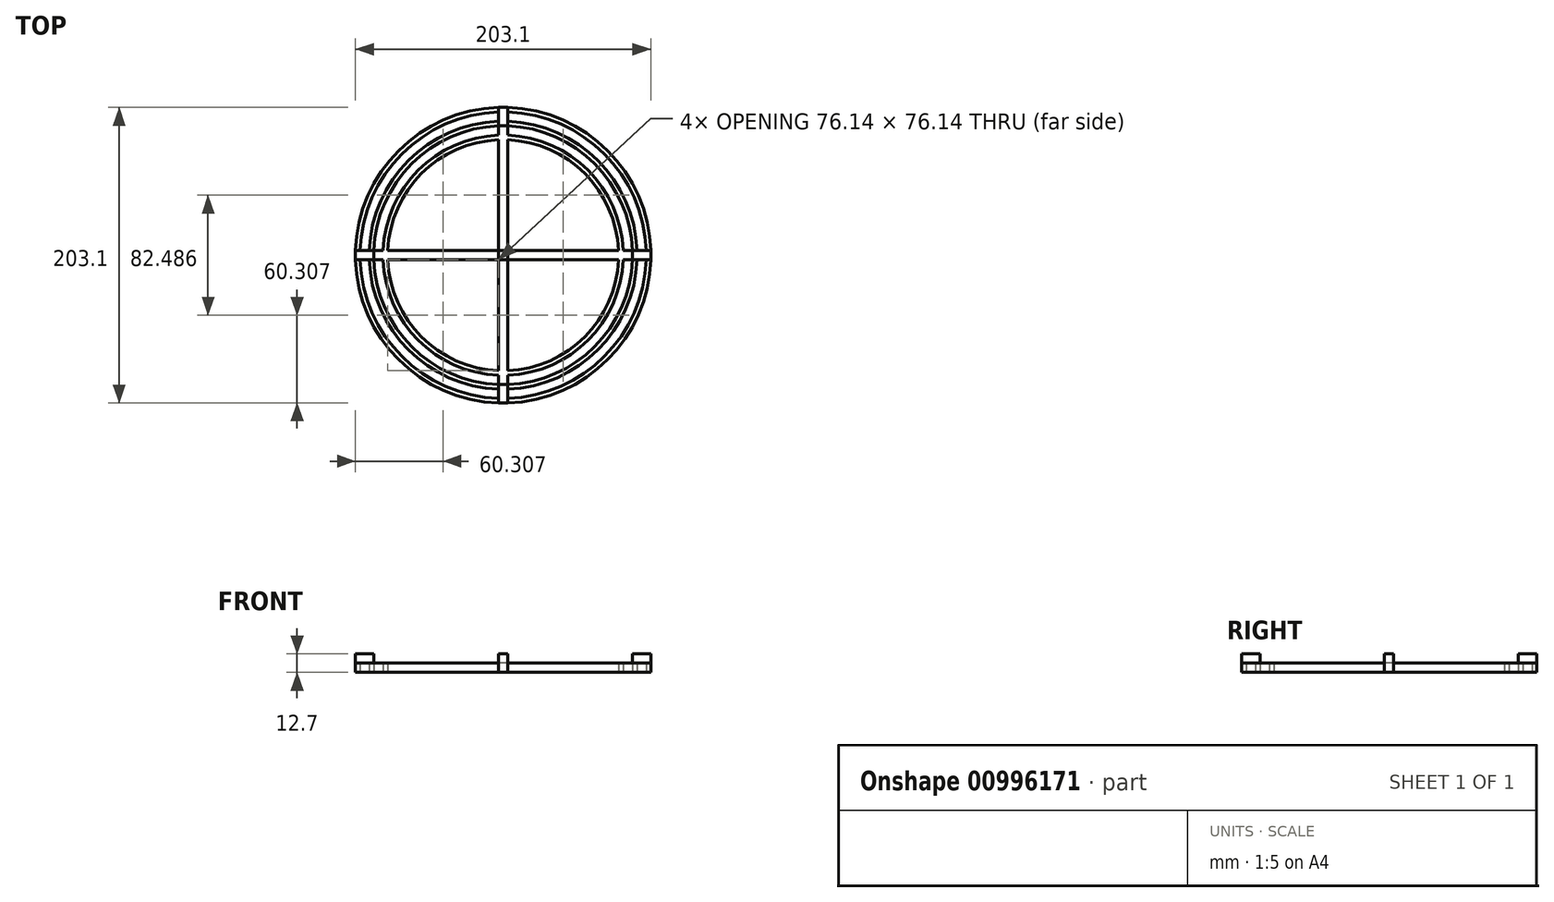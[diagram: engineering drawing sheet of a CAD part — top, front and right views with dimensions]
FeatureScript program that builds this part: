
annotation { "Feature Type Name" : "Feature", "Feature Type Description" : "" }
export const myFeature = defineFeature(function(context is Context, id is Id, definition is map)
    precondition{}
    {
        {
            var Q0;
            Q0=qCreatedBy(makeId("Top.planeOp"),FACE);
            var sketch = newSketch(context, id + "F0", { "sketchPlane" : qUnion([Q0])});
            skCircle(sketch, "E0", {"center": v(0, 0) * mm, "radius": 101.6 * mm});
            skCircle(sketch, "E1", {"center": v(0, 0) * mm, "radius": 98.43 * mm});
            skCircle(sketch, "E2", {"center": v(0, 0) * mm, "radius": 92.08 * mm});
            skCircle(sketch, "E3", {"center": v(0, 0) * mm, "radius": 88.9 * mm});
            skCircle(sketch, "E4", {"center": v(0, 0) * mm, "radius": 82.55 * mm});
            skCircle(sketch, "E5", {"center": v(0, 0) * mm, "radius": 79.38 * mm});
            skLineSegment(sketch, "E6.bottom", {"start": v(3.18, 101.55) * mm, "end": v(-3.18, 101.55) * mm});
            skLineSegment(sketch, "E6.top", {"start": v(3.18, -101.55) * mm, "end": v(-3.18, -101.55) * mm});
            skLineSegment(sketch, "E6.left", {"start": v(3.18, 101.55) * mm, "end": v(3.18, -101.55) * mm});
            skLineSegment(sketch, "E6.right", {"start": v(-3.18, 101.55) * mm, "end": v(-3.18, -101.55) * mm});
            skLineSegment(sketch, "E7.bottom", {"start": v(-101.55, 3.18) * mm, "end": v(101.55, 3.18) * mm});
            skLineSegment(sketch, "E7.top", {"start": v(-101.55, -3.18) * mm, "end": v(101.55, -3.18) * mm});
            skLineSegment(sketch, "E7.left", {"start": v(-101.55, 3.18) * mm, "end": v(-101.55, -3.18) * mm});
            skLineSegment(sketch, "E7.right", {"start": v(101.55, 3.18) * mm, "end": v(101.55, -3.18) * mm});
            skSolve(sketch);
        }
        {
            var Q0;
            {var subQ3=sQuery(id+"F0.wireOp",EDGE,"E7.top");var subQ5=sQuery(id+"F0.wireOp",EDGE,"E1");var subQ6=makeQuery(id+"F0.imprint","INTERSECT",VERTEX,{"disambiguationData":[OD(0.0)],"derivedFrom":[subQ5,subQ3]});Q0=makeQuery(id+"F0.imprint","IMPRINT",FACE,{"disambiguationData":[TD([[makeQuery(id+"F0.imprint","IMPRINT",EDGE,{"disambiguationData":[TD([[subQ6,-1.0]])],"derivedFrom":subQ5}),-1.0]])]});}
            var Q1;
            {var subQ0=sQuery(id+"F0.wireOp",EDGE,"E6.right");var subQ5=sQuery(id+"F0.wireOp",EDGE,"E1");var subQ6=makeQuery(id+"F0.imprint","INTERSECT",VERTEX,{"disambiguationData":[OD(0.0)],"derivedFrom":[subQ5,subQ0]});Q1=makeQuery(id+"F0.imprint","IMPRINT",FACE,{"disambiguationData":[TD([[makeQuery(id+"F0.imprint","IMPRINT",EDGE,{"disambiguationData":[TD([[subQ6,-1.0]])],"derivedFrom":subQ5}),-1.0]])]});}
            var Q2;
            {var subQ5=sQuery(id+"F0.wireOp",EDGE,"E7.left");Q2=makeQuery(id+"F0.imprint","IMPRINT",FACE,{"disambiguationData":[TD([[makeQuery(id+"F0.imprint","IMPRINT",EDGE,{"derivedFrom":subQ5}),1.0]])]});}
            var Q3;
            {var subQ0=sQuery(id+"F0.wireOp",EDGE,"E7.bottom");var subQ1=sQuery(id+"F0.wireOp",EDGE,"E1");var subQ2=makeQuery(id+"F0.imprint","INTERSECT",VERTEX,{"disambiguationData":[OD(1.0)],"derivedFrom":[subQ1,subQ0]});Q3=makeQuery(id+"F0.imprint","IMPRINT",FACE,{"disambiguationData":[TD([[makeQuery(id+"F0.imprint","IMPRINT",EDGE,{"disambiguationData":[TD([[subQ2,-1.0]])],"derivedFrom":subQ1}),1.0]])]});}
            var Q4;
            {var subQ0=sQuery(id+"F0.wireOp",EDGE,"E7.bottom");var subQ1=sQuery(id+"F0.wireOp",EDGE,"E2");var subQ2=makeQuery(id+"F0.imprint","INTERSECT",VERTEX,{"disambiguationData":[OD(1.0)],"derivedFrom":[subQ1,subQ0]});Q4=makeQuery(id+"F0.imprint","IMPRINT",FACE,{"disambiguationData":[TD([[makeQuery(id+"F0.imprint","IMPRINT",EDGE,{"disambiguationData":[TD([[subQ2,-1.0]])],"derivedFrom":subQ1}),1.0]])]});}
            var Q5;
            {var subQ0=sQuery(id+"F0.wireOp",EDGE,"E7.bottom");var subQ1=sQuery(id+"F0.wireOp",EDGE,"E4");var subQ2=makeQuery(id+"F0.imprint","INTERSECT",VERTEX,{"disambiguationData":[OD(1.0)],"derivedFrom":[subQ1,subQ0]});Q5=makeQuery(id+"F0.imprint","IMPRINT",FACE,{"disambiguationData":[TD([[makeQuery(id+"F0.imprint","IMPRINT",EDGE,{"disambiguationData":[TD([[subQ2,-1.0]])],"derivedFrom":subQ1}),1.0]])]});}
            var Q6;
            {var subQ0=sQuery(id+"F0.wireOp",EDGE,"E7.bottom");var subQ1=sQuery(id+"F0.wireOp",EDGE,"E3");var subQ2=makeQuery(id+"F0.imprint","INTERSECT",VERTEX,{"disambiguationData":[OD(1.0)],"derivedFrom":[subQ1,subQ0]});Q6=makeQuery(id+"F0.imprint","IMPRINT",FACE,{"disambiguationData":[TD([[makeQuery(id+"F0.imprint","IMPRINT",EDGE,{"disambiguationData":[TD([[subQ2,-1.0]])],"derivedFrom":subQ1}),1.0]])]});}
            var Q7;
            {var subQ0=sQuery(id+"F0.wireOp",EDGE,"E7.bottom");var subQ1=sQuery(id+"F0.wireOp",EDGE,"E5");var subQ2=makeQuery(id+"F0.imprint","INTERSECT",VERTEX,{"disambiguationData":[OD(1.0)],"derivedFrom":[subQ1,subQ0]});Q7=makeQuery(id+"F0.imprint","IMPRINT",FACE,{"disambiguationData":[TD([[makeQuery(id+"F0.imprint","IMPRINT",EDGE,{"disambiguationData":[TD([[subQ2,-1.0]])],"derivedFrom":subQ1}),1.0]])]});}
            var Q8;
            {var subQ0=sQuery(id+"F0.wireOp",EDGE,"E7.bottom");var subQ1=sQuery(id+"F0.wireOp",EDGE,"E5");var subQ2=makeQuery(id+"F0.imprint","INTERSECT",VERTEX,{"disambiguationData":[OD(0.0)],"derivedFrom":[subQ1,subQ0]});Q8=makeQuery(id+"F0.imprint","IMPRINT",FACE,{"disambiguationData":[TD([[makeQuery(id+"F0.imprint","IMPRINT",EDGE,{"disambiguationData":[TD([[subQ2,1.0]])],"derivedFrom":subQ1}),1.0]])]});}
            var Q9;
            {var subQ0=sQuery(id+"F0.wireOp",EDGE,"E6.right");var subQ1=sQuery(id+"F0.wireOp",EDGE,"E5");var subQ2=makeQuery(id+"F0.imprint","INTERSECT",VERTEX,{"disambiguationData":[OD(1.0)],"derivedFrom":[subQ1,subQ0]});Q9=makeQuery(id+"F0.imprint","IMPRINT",FACE,{"disambiguationData":[TD([[makeQuery(id+"F0.imprint","IMPRINT",EDGE,{"disambiguationData":[TD([[subQ2,-1.0]])],"derivedFrom":subQ1}),1.0]])]});}
            var Q10;
            {var subQ0=sQuery(id+"F0.wireOp",EDGE,"E6.left");var subQ1=sQuery(id+"F0.wireOp",EDGE,"E5");var subQ2=makeQuery(id+"F0.imprint","INTERSECT",VERTEX,{"disambiguationData":[OD(0.0)],"derivedFrom":[subQ1,subQ0]});Q10=makeQuery(id+"F0.imprint","IMPRINT",FACE,{"disambiguationData":[TD([[makeQuery(id+"F0.imprint","IMPRINT",EDGE,{"disambiguationData":[TD([[subQ2,-1.0]])],"derivedFrom":subQ1}),1.0]])]});}
            var Q11;
            {var subQ0=sQuery(id+"F0.wireOp",EDGE,"E7.bottom");var subQ1=sQuery(id+"F0.wireOp",EDGE,"E6.left");var subQ2=makeQuery(id+"F0.imprint","INTERSECT",VERTEX,{"derivedFrom":[subQ1,subQ0]});Q11=makeQuery(id+"F0.imprint","IMPRINT",FACE,{"disambiguationData":[TD([[makeQuery(id+"F0.imprint","IMPRINT",EDGE,{"disambiguationData":[TD([[subQ2,-1.0]])],"derivedFrom":subQ1}),-1.0]])]});}
            var Q12;
            {var subQ0=sQuery(id+"F0.wireOp",EDGE,"E7.bottom");var subQ1=sQuery(id+"F0.wireOp",EDGE,"E4");var subQ2=makeQuery(id+"F0.imprint","INTERSECT",VERTEX,{"disambiguationData":[OD(0.0)],"derivedFrom":[subQ1,subQ0]});Q12=makeQuery(id+"F0.imprint","IMPRINT",FACE,{"disambiguationData":[TD([[makeQuery(id+"F0.imprint","IMPRINT",EDGE,{"disambiguationData":[TD([[subQ2,1.0]])],"derivedFrom":subQ1}),1.0]])]});}
            var Q13;
            {var subQ0=sQuery(id+"F0.wireOp",EDGE,"E7.bottom");var subQ1=sQuery(id+"F0.wireOp",EDGE,"E3");var subQ2=makeQuery(id+"F0.imprint","INTERSECT",VERTEX,{"disambiguationData":[OD(0.0)],"derivedFrom":[subQ1,subQ0]});Q13=makeQuery(id+"F0.imprint","IMPRINT",FACE,{"disambiguationData":[TD([[makeQuery(id+"F0.imprint","IMPRINT",EDGE,{"disambiguationData":[TD([[subQ2,1.0]])],"derivedFrom":subQ1}),1.0]])]});}
            var Q14;
            {var subQ0=sQuery(id+"F0.wireOp",EDGE,"E7.bottom");var subQ1=sQuery(id+"F0.wireOp",EDGE,"E2");var subQ2=makeQuery(id+"F0.imprint","INTERSECT",VERTEX,{"disambiguationData":[OD(0.0)],"derivedFrom":[subQ1,subQ0]});Q14=makeQuery(id+"F0.imprint","IMPRINT",FACE,{"disambiguationData":[TD([[makeQuery(id+"F0.imprint","IMPRINT",EDGE,{"disambiguationData":[TD([[subQ2,1.0]])],"derivedFrom":subQ1}),1.0]])]});}
            var Q15;
            {var subQ0=sQuery(id+"F0.wireOp",EDGE,"E7.bottom");var subQ1=sQuery(id+"F0.wireOp",EDGE,"E1");var subQ2=makeQuery(id+"F0.imprint","INTERSECT",VERTEX,{"disambiguationData":[OD(0.0)],"derivedFrom":[subQ1,subQ0]});Q15=makeQuery(id+"F0.imprint","IMPRINT",FACE,{"disambiguationData":[TD([[makeQuery(id+"F0.imprint","IMPRINT",EDGE,{"disambiguationData":[TD([[subQ2,1.0]])],"derivedFrom":subQ1}),1.0]])]});}
            var Q16;
            {var subQ5=sQuery(id+"F0.wireOp",EDGE,"E7.right");Q16=makeQuery(id+"F0.imprint","IMPRINT",FACE,{"disambiguationData":[TD([[makeQuery(id+"F0.imprint","IMPRINT",EDGE,{"derivedFrom":subQ5}),-1.0]])]});}
            var Q17;
            {var subQ5=sQuery(id+"F0.wireOp",EDGE,"E6.top");Q17=makeQuery(id+"F0.imprint","IMPRINT",FACE,{"disambiguationData":[TD([[makeQuery(id+"F0.imprint","IMPRINT",EDGE,{"derivedFrom":subQ5}),-1.0]])]});}
            var Q18;
            {var subQ0=sQuery(id+"F0.wireOp",EDGE,"E6.right");var subQ1=sQuery(id+"F0.wireOp",EDGE,"E2");var subQ2=makeQuery(id+"F0.imprint","INTERSECT",VERTEX,{"disambiguationData":[OD(1.0)],"derivedFrom":[subQ1,subQ0]});Q18=makeQuery(id+"F0.imprint","IMPRINT",FACE,{"disambiguationData":[TD([[makeQuery(id+"F0.imprint","IMPRINT",EDGE,{"disambiguationData":[TD([[subQ2,-1.0]])],"derivedFrom":subQ1}),1.0]])]});}
            var Q19;
            {var subQ0=sQuery(id+"F0.wireOp",EDGE,"E6.right");var subQ1=sQuery(id+"F0.wireOp",EDGE,"E4");var subQ2=makeQuery(id+"F0.imprint","INTERSECT",VERTEX,{"disambiguationData":[OD(1.0)],"derivedFrom":[subQ1,subQ0]});Q19=makeQuery(id+"F0.imprint","IMPRINT",FACE,{"disambiguationData":[TD([[makeQuery(id+"F0.imprint","IMPRINT",EDGE,{"disambiguationData":[TD([[subQ2,-1.0]])],"derivedFrom":subQ1}),1.0]])]});}
            var Q20;
            {var subQ0=sQuery(id+"F0.wireOp",EDGE,"E6.left");var subQ5=sQuery(id+"F0.wireOp",EDGE,"E1");var subQ7=makeQuery(id+"F0.imprint","INTERSECT",VERTEX,{"disambiguationData":[OD(1.0)],"derivedFrom":[subQ5,subQ0]});Q20=makeQuery(id+"F0.imprint","IMPRINT",FACE,{"disambiguationData":[TD([[makeQuery(id+"F0.imprint","IMPRINT",EDGE,{"disambiguationData":[TD([[subQ7,-1.0]])],"derivedFrom":subQ5}),-1.0]])]});}
            var Q21;
            {var subQ0=sQuery(id+"F0.wireOp",EDGE,"E6.left");var subQ1=sQuery(id+"F0.wireOp",EDGE,"E2");var subQ2=makeQuery(id+"F0.imprint","INTERSECT",VERTEX,{"disambiguationData":[OD(1.0)],"derivedFrom":[subQ1,subQ0]});Q21=makeQuery(id+"F0.imprint","IMPRINT",FACE,{"disambiguationData":[TD([[makeQuery(id+"F0.imprint","IMPRINT",EDGE,{"disambiguationData":[TD([[subQ2,-1.0]])],"derivedFrom":subQ1}),1.0]])]});}
            var Q22;
            {var subQ0=sQuery(id+"F0.wireOp",EDGE,"E6.left");var subQ1=sQuery(id+"F0.wireOp",EDGE,"E4");var subQ2=makeQuery(id+"F0.imprint","INTERSECT",VERTEX,{"disambiguationData":[OD(1.0)],"derivedFrom":[subQ1,subQ0]});Q22=makeQuery(id+"F0.imprint","IMPRINT",FACE,{"disambiguationData":[TD([[makeQuery(id+"F0.imprint","IMPRINT",EDGE,{"disambiguationData":[TD([[subQ2,-1.0]])],"derivedFrom":subQ1}),1.0]])]});}
            var Q23;
            {var subQ0=sQuery(id+"F0.wireOp",EDGE,"E7.top");var subQ1=sQuery(id+"F0.wireOp",EDGE,"E2");var subQ2=makeQuery(id+"F0.imprint","INTERSECT",VERTEX,{"disambiguationData":[OD(0.0)],"derivedFrom":[subQ1,subQ0]});Q23=makeQuery(id+"F0.imprint","IMPRINT",FACE,{"disambiguationData":[TD([[makeQuery(id+"F0.imprint","IMPRINT",EDGE,{"disambiguationData":[TD([[subQ2,-1.0]])],"derivedFrom":subQ1}),1.0]])]});}
            var Q24;
            {var subQ0=sQuery(id+"F0.wireOp",EDGE,"E7.top");var subQ1=sQuery(id+"F0.wireOp",EDGE,"E4");var subQ2=makeQuery(id+"F0.imprint","INTERSECT",VERTEX,{"disambiguationData":[OD(0.0)],"derivedFrom":[subQ1,subQ0]});Q24=makeQuery(id+"F0.imprint","IMPRINT",FACE,{"disambiguationData":[TD([[makeQuery(id+"F0.imprint","IMPRINT",EDGE,{"disambiguationData":[TD([[subQ2,-1.0]])],"derivedFrom":subQ1}),1.0]])]});}
            var Q25;
            {var subQ0=sQuery(id+"F0.wireOp",EDGE,"E6.right");var subQ1=sQuery(id+"F0.wireOp",EDGE,"E4");var subQ2=makeQuery(id+"F0.imprint","INTERSECT",VERTEX,{"disambiguationData":[OD(0.0)],"derivedFrom":[subQ1,subQ0]});Q25=makeQuery(id+"F0.imprint","IMPRINT",FACE,{"disambiguationData":[TD([[makeQuery(id+"F0.imprint","IMPRINT",EDGE,{"disambiguationData":[TD([[subQ2,-1.0]])],"derivedFrom":subQ1}),1.0]])]});}
            var Q26;
            {var subQ0=sQuery(id+"F0.wireOp",EDGE,"E6.right");var subQ1=sQuery(id+"F0.wireOp",EDGE,"E2");var subQ2=makeQuery(id+"F0.imprint","INTERSECT",VERTEX,{"disambiguationData":[OD(0.0)],"derivedFrom":[subQ1,subQ0]});Q26=makeQuery(id+"F0.imprint","IMPRINT",FACE,{"disambiguationData":[TD([[makeQuery(id+"F0.imprint","IMPRINT",EDGE,{"disambiguationData":[TD([[subQ2,-1.0]])],"derivedFrom":subQ1}),1.0]])]});}
            var Q27;
            {var subQ0=sQuery(id+"F0.wireOp",EDGE,"E6.left");var subQ1=sQuery(id+"F0.wireOp",EDGE,"E4");var subQ2=makeQuery(id+"F0.imprint","INTERSECT",VERTEX,{"disambiguationData":[OD(0.0)],"derivedFrom":[subQ1,subQ0]});Q27=makeQuery(id+"F0.imprint","IMPRINT",FACE,{"disambiguationData":[TD([[makeQuery(id+"F0.imprint","IMPRINT",EDGE,{"disambiguationData":[TD([[subQ2,-1.0]])],"derivedFrom":subQ1}),1.0]])]});}
            var Q28;
            {var subQ0=sQuery(id+"F0.wireOp",EDGE,"E6.left");var subQ1=sQuery(id+"F0.wireOp",EDGE,"E2");var subQ2=makeQuery(id+"F0.imprint","INTERSECT",VERTEX,{"disambiguationData":[OD(0.0)],"derivedFrom":[subQ1,subQ0]});Q28=makeQuery(id+"F0.imprint","IMPRINT",FACE,{"disambiguationData":[TD([[makeQuery(id+"F0.imprint","IMPRINT",EDGE,{"disambiguationData":[TD([[subQ2,-1.0]])],"derivedFrom":subQ1}),1.0]])]});}
            var Q29;
            {var subQ5=sQuery(id+"F0.wireOp",EDGE,"E6.bottom");Q29=makeQuery(id+"F0.imprint","IMPRINT",FACE,{"disambiguationData":[TD([[makeQuery(id+"F0.imprint","IMPRINT",EDGE,{"derivedFrom":subQ5}),1.0]])]});}
            var Q30;
            {var subQ0=sQuery(id+"F0.wireOp",EDGE,"E6.left");var subQ5=sQuery(id+"F0.wireOp",EDGE,"E1");var subQ6=makeQuery(id+"F0.imprint","INTERSECT",VERTEX,{"disambiguationData":[OD(0.0)],"derivedFrom":[subQ5,subQ0]});Q30=makeQuery(id+"F0.imprint","IMPRINT",FACE,{"disambiguationData":[TD([[makeQuery(id+"F0.imprint","IMPRINT",EDGE,{"disambiguationData":[TD([[subQ6,1.0]])],"derivedFrom":subQ5}),-1.0]])]});}
            var Q31;
            {var subQ0=sQuery(id+"F0.wireOp",EDGE,"E6.left");var subQ1=sQuery(id+"F0.wireOp",EDGE,"E2");var subQ2=makeQuery(id+"F0.imprint","INTERSECT",VERTEX,{"disambiguationData":[OD(0.0)],"derivedFrom":[subQ1,subQ0]});Q31=makeQuery(id+"F0.imprint","IMPRINT",FACE,{"disambiguationData":[TD([[makeQuery(id+"F0.imprint","IMPRINT",EDGE,{"disambiguationData":[TD([[subQ2,1.0]])],"derivedFrom":subQ1}),1.0]])]});}
            var Q32;
            {var subQ0=sQuery(id+"F0.wireOp",EDGE,"E6.left");var subQ1=sQuery(id+"F0.wireOp",EDGE,"E4");var subQ2=makeQuery(id+"F0.imprint","INTERSECT",VERTEX,{"disambiguationData":[OD(0.0)],"derivedFrom":[subQ1,subQ0]});Q32=makeQuery(id+"F0.imprint","IMPRINT",FACE,{"disambiguationData":[TD([[makeQuery(id+"F0.imprint","IMPRINT",EDGE,{"disambiguationData":[TD([[subQ2,1.0]])],"derivedFrom":subQ1}),1.0]])]});}
            var Q33;
            {var subQ0=sQuery(id+"F0.wireOp",EDGE,"E6.right");var subQ1=sQuery(id+"F0.wireOp",EDGE,"E3");var subQ2=makeQuery(id+"F0.imprint","INTERSECT",VERTEX,{"disambiguationData":[OD(1.0)],"derivedFrom":[subQ1,subQ0]});Q33=makeQuery(id+"F0.imprint","IMPRINT",FACE,{"disambiguationData":[TD([[makeQuery(id+"F0.imprint","IMPRINT",EDGE,{"disambiguationData":[TD([[subQ2,-1.0]])],"derivedFrom":subQ1}),1.0]])]});}
            var Q34;
            {var subQ0=sQuery(id+"F0.wireOp",EDGE,"E6.right");var subQ1=sQuery(id+"F0.wireOp",EDGE,"E1");var subQ2=makeQuery(id+"F0.imprint","INTERSECT",VERTEX,{"disambiguationData":[OD(1.0)],"derivedFrom":[subQ1,subQ0]});Q34=makeQuery(id+"F0.imprint","IMPRINT",FACE,{"disambiguationData":[TD([[makeQuery(id+"F0.imprint","IMPRINT",EDGE,{"disambiguationData":[TD([[subQ2,-1.0]])],"derivedFrom":subQ1}),1.0]])]});}
            var Q35;
            {var subQ0=sQuery(id+"F0.wireOp",EDGE,"E6.left");var subQ1=sQuery(id+"F0.wireOp",EDGE,"E3");var subQ2=makeQuery(id+"F0.imprint","INTERSECT",VERTEX,{"disambiguationData":[OD(0.0)],"derivedFrom":[subQ1,subQ0]});Q35=makeQuery(id+"F0.imprint","IMPRINT",FACE,{"disambiguationData":[TD([[makeQuery(id+"F0.imprint","IMPRINT",EDGE,{"disambiguationData":[TD([[subQ2,-1.0]])],"derivedFrom":subQ1}),1.0]])]});}
            var Q36;
            {var subQ0=sQuery(id+"F0.wireOp",EDGE,"E6.left");var subQ1=sQuery(id+"F0.wireOp",EDGE,"E1");var subQ2=makeQuery(id+"F0.imprint","INTERSECT",VERTEX,{"disambiguationData":[OD(0.0)],"derivedFrom":[subQ1,subQ0]});Q36=makeQuery(id+"F0.imprint","IMPRINT",FACE,{"disambiguationData":[TD([[makeQuery(id+"F0.imprint","IMPRINT",EDGE,{"disambiguationData":[TD([[subQ2,-1.0]])],"derivedFrom":subQ1}),1.0]])]});}
            extrude(context, id + "F1", {"entities" : qUnion([Q0, Q1, Q2, Q3, Q4, Q5, Q6, Q7, Q8, Q9, Q10, Q11, Q12, Q13, Q14, Q15, Q16, Q17, Q18, Q19, Q20, Q21, Q22, Q23, Q24, Q25, Q26, Q27, Q28, Q29, Q30, Q31, Q32, Q33, Q34, Q35, Q36]), "depth" : 6.35 * mm, "offsetDistance" : 25.4 * mm});
        }
        {
            var Q0;
            Q0=makeQuery(id+"F1.opExtrude","CAP_FACE",FACE,{"disambiguationData":[OSD([sQuery(id+"F0.wireOp",EDGE,"E0"),sQuery(id+"F0.wireOp",EDGE,"E1"),sQuery(id+"F0.wireOp",EDGE,"E2"),sQuery(id+"F0.wireOp",EDGE,"E3"),sQuery(id+"F0.wireOp",EDGE,"E4"),sQuery(id+"F0.wireOp",EDGE,"E5"),sQuery(id+"F0.wireOp",EDGE,"E6.bottom"),sQuery(id+"F0.wireOp",EDGE,"E6.top"),sQuery(id+"F0.wireOp",EDGE,"E6.left"),sQuery(id+"F0.wireOp",EDGE,"E6.right"),sQuery(id+"F0.wireOp",EDGE,"E7.bottom"),sQuery(id+"F0.wireOp",EDGE,"E7.top"),sQuery(id+"F0.wireOp",EDGE,"E7.left"),sQuery(id+"F0.wireOp",EDGE,"E7.right")])],"isStart":false});
            var sketch = newSketch(context, id + "F2", { "sketchPlane" : qUnion([Q0])});
            skLineSegment(sketch, "E8.bottom", {"start": v(-88.84, 3.18) * mm, "end": v(-101.55, 3.18) * mm});
            skLineSegment(sketch, "E8.top", {"start": v(-88.84, -3.17) * mm, "end": v(-101.55, -3.17) * mm});
            skLineSegment(sketch, "E8.left", {"start": v(-88.84, 3.18) * mm, "end": v(-88.84, -3.17) * mm});
            skLineSegment(sketch, "E8.right", {"start": v(-101.55, 3.18) * mm, "end": v(-101.55, -3.17) * mm});
            skLineSegment(sketch, "E9.bottom", {"start": v(88.84, 3.18) * mm, "end": v(101.55, 3.18) * mm});
            skLineSegment(sketch, "E9.top", {"start": v(88.84, -3.18) * mm, "end": v(101.55, -3.18) * mm});
            skLineSegment(sketch, "E9.left", {"start": v(88.84, 3.18) * mm, "end": v(88.84, -3.18) * mm});
            skLineSegment(sketch, "E9.right", {"start": v(101.55, 3.18) * mm, "end": v(101.55, -3.18) * mm});
            skLineSegment(sketch, "E10.bottom", {"start": v(3.18, 88.84) * mm, "end": v(-3.18, 88.84) * mm});
            skLineSegment(sketch, "E10.top", {"start": v(3.18, 101.55) * mm, "end": v(-3.18, 101.55) * mm});
            skLineSegment(sketch, "E10.left", {"start": v(3.18, 88.84) * mm, "end": v(3.18, 101.55) * mm});
            skLineSegment(sketch, "E10.right", {"start": v(-3.18, 88.84) * mm, "end": v(-3.18, 101.55) * mm});
            skLineSegment(sketch, "E11.bottom", {"start": v(3.17, -88.84) * mm, "end": v(-3.17, -88.84) * mm});
            skLineSegment(sketch, "E11.top", {"start": v(3.17, -101.55) * mm, "end": v(-3.17, -101.55) * mm});
            skLineSegment(sketch, "E11.left", {"start": v(3.17, -88.84) * mm, "end": v(3.17, -101.55) * mm});
            skLineSegment(sketch, "E11.right", {"start": v(-3.17, -88.84) * mm, "end": v(-3.17, -101.55) * mm});
            skLineSegment(sketch, "E12.bottom", {"start": v(-3.18, 3.18) * mm, "end": v(3.18, 3.18) * mm});
            skLineSegment(sketch, "E12.top", {"start": v(-3.18, -3.18) * mm, "end": v(3.18, -3.18) * mm});
            skLineSegment(sketch, "E12.left", {"start": v(-3.18, 3.18) * mm, "end": v(-3.18, -3.18) * mm});
            skLineSegment(sketch, "E12.right", {"start": v(3.18, 3.18) * mm, "end": v(3.18, -3.18) * mm});
            skSolve(sketch);
        }
        {
            var Q0;
            Q0 = qSketchRegion(id + "F2", true);
            extrude(context, id + "F3", {"entities" : qUnion([Q0]), "operationType" : NewBodyOperationType.ADD, "depth" : 6.35 * mm, "offsetDistance" : 25.4 * mm});
        }
    });
